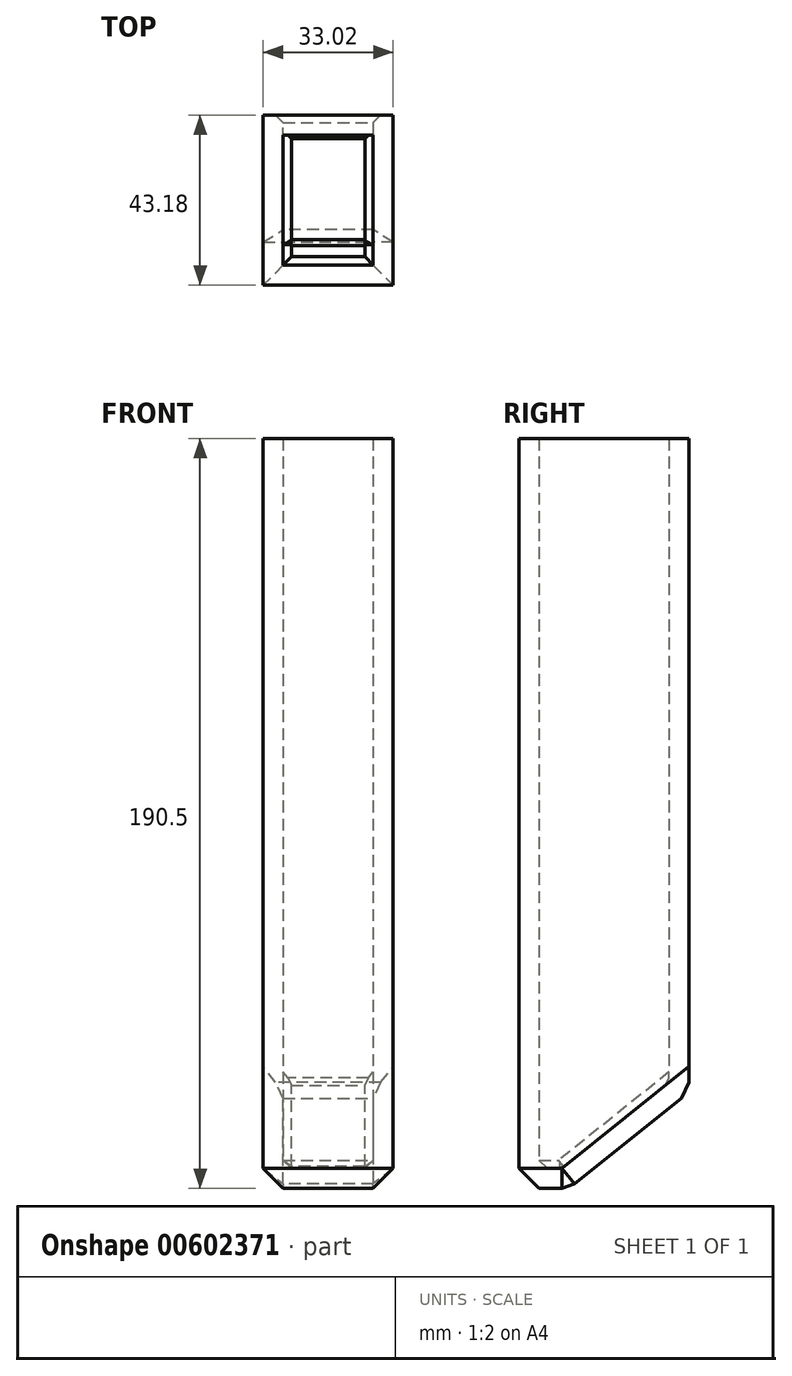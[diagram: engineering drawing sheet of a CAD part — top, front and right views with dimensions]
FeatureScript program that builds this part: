
annotation { "Feature Type Name" : "Feature", "Feature Type Description" : "" }
export const myFeature = defineFeature(function(context is Context, id is Id, definition is map)
    precondition{}
    {
        {
            var Q0;
            Q0=qCreatedBy(makeId("Top.planeOp"),FACE);
            var sketch = newSketch(context, id + "F0", { "sketchPlane" : qUnion([Q0])});
            skLineSegment(sketch, "E0.bottom", {"start": v(16.51, 21.59) * mm, "end": v(-16.51, 21.59) * mm});
            skLineSegment(sketch, "E0.top", {"start": v(16.51, -21.59) * mm, "end": v(-16.51, -21.59) * mm});
            skLineSegment(sketch, "E0.left", {"start": v(16.51, 21.6) * mm, "end": v(16.51, -21.59) * mm});
            skLineSegment(sketch, "E0.right", {"start": v(-16.51, 21.6) * mm, "end": v(-16.51, -21.59) * mm});
            skPoint(sketch, "E0.middle", {"position": v(0, 0) * mm});
            skSolve(sketch);
        }
        {
            var Q0;
            Q0 = qSketchRegion(id + "F0", true);
            extrude(context, id + "F1", {"entities" : qUnion([Q0]), "depth" : 190.5 * mm, "offsetDistance" : 25.4 * mm});
        }
        {
            var Q0;
            Q0=makeQuery(id+"F1.opExtrude","SWEPT_FACE",FACE,{"disambiguationData":[OSD([sQuery(id+"F0.wireOp",EDGE,"E0.left")])]});
            var sketch = newSketch(context, id + "F2", { "sketchPlane" : qUnion([Q0])});
            skLineSegment(sketch, "E1", {"start": v(-8.92, 0) * mm, "end": v(21.6, 24.44) * mm});
            skLineSegment(sketch, "E2", {"start": v(21.6, 24.44) * mm, "end": v(21.6, 0) * mm});
            skLineSegment(sketch, "E3", {"start": v(21.6, 0) * mm, "end": v(-8.92, 0) * mm});
            skSolve(sketch);
        }
        {
            var Q0;
            Q0 = qSketchRegion(id + "F2", true);
            extrude(context, id + "F3", {"entities" : qUnion([Q0]), "operationType" : NewBodyOperationType.REMOVE, "oppositeDirection" : true, "depth" : 50.8 * mm, "offsetDistance" : 25.4 * mm});
        }
        {
            var Q0;
            Q0=makeQuery(id+"F3.boolean.opBoolean","COPY",FACE,{"derivedFrom":makeQuery(id+"F3.opExtrude","SWEPT_FACE",FACE,{"disambiguationData":[OSD([sQuery(id+"F2.wireOp",EDGE,"E1")])]})});
            var Q1;
            Q1=makeQuery(id+"F1.opExtrude","CAP_FACE",FACE,{"disambiguationData":[OSD([sQuery(id+"F0.wireOp",EDGE,"E0.bottom"),sQuery(id+"F0.wireOp",EDGE,"E0.top"),sQuery(id+"F0.wireOp",EDGE,"E0.left"),sQuery(id+"F0.wireOp",EDGE,"E0.right")])],"isStart":true});
            chamfer(context, id + "F4", {"entities" : qUnion([Q0, Q1]), "width" : 5.08 * mm, "tangentPropagation" : true});
        }
        {
            var Q0;
            Q0=makeQuery(id+"F1.opExtrude","CAP_FACE",FACE,{"disambiguationData":[OSD([sQuery(id+"F0.wireOp",EDGE,"E0.bottom"),sQuery(id+"F0.wireOp",EDGE,"E0.top"),sQuery(id+"F0.wireOp",EDGE,"E0.left"),sQuery(id+"F0.wireOp",EDGE,"E0.right")])],"isStart":false});
            shell(context, id + "F5", {"entities" : qUnion([Q0]), "thickness" : 5.08 * mm});
        }
    });
